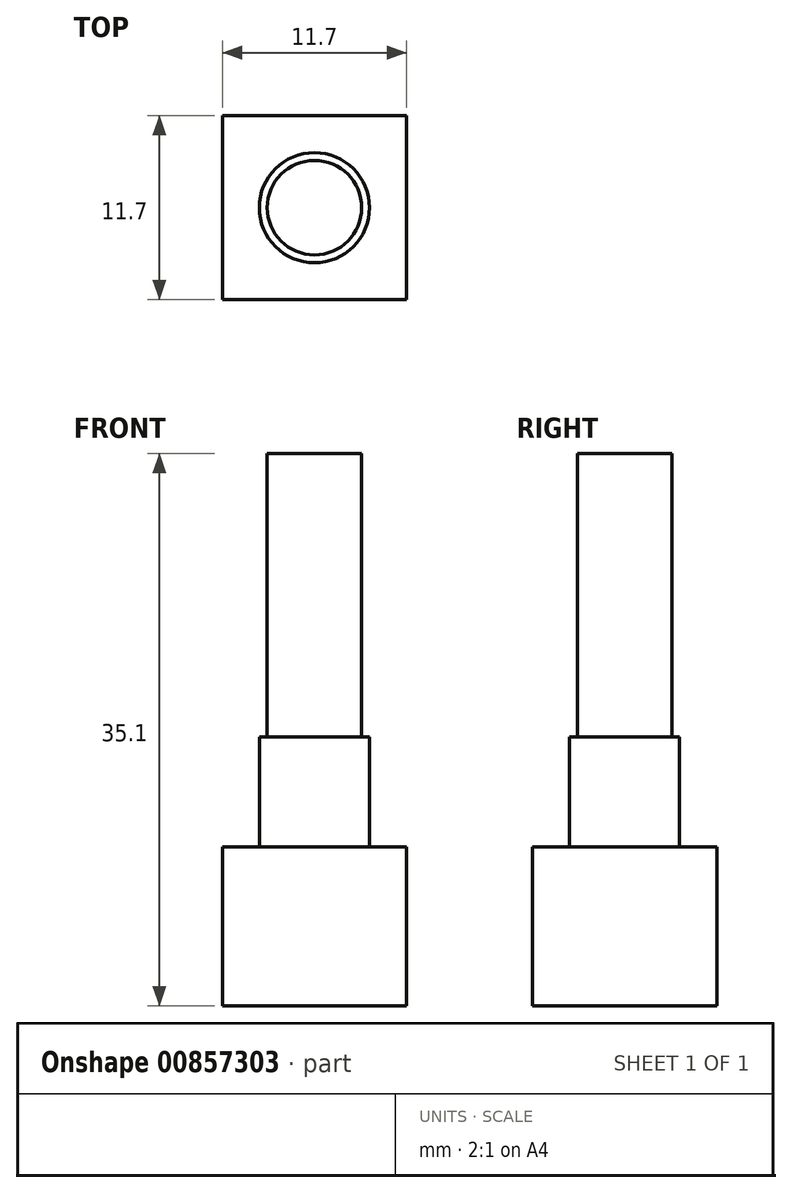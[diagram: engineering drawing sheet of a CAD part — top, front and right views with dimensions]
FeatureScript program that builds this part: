
annotation { "Feature Type Name" : "Feature", "Feature Type Description" : "" }
export const myFeature = defineFeature(function(context is Context, id is Id, definition is map)
    precondition{}
    {
        {
            var Q0;
            Q0=qCreatedBy(makeId("Top.planeOp"),FACE);
            var sketch = newSketch(context, id + "F0", { "sketchPlane" : qUnion([Q0])});
            skCircle(sketch, "E0", {"center": v(0, 0) * mm, "radius": 3 * mm});
            skSolve(sketch);
        }
        {
            var Q0;
            Q0 = qSketchRegion(id + "F0", true);
            extrude(context, id + "F1", {"entities" : qUnion([Q0]), "depth" : (7 + 11) * mm, "offsetDistance" : 25 * mm});
        }
        {
            var Q0;
            Q0=makeQuery(id+"F1.opExtrude","CAP_FACE",FACE,{"disambiguationData":[OSD([sQuery(id+"F0.wireOp",EDGE,"E0")])],"isStart":true});
            var sketch = newSketch(context, id + "F2", { "sketchPlane" : qUnion([Q0])});
            skCircle(sketch, "E1", {"center": v(0, 0) * mm, "radius": 3.5 * mm});
            skSolve(sketch);
        }
        {
            var Q0;
            Q0=makeQuery(id+"F2.imprint","IMPRINT",FACE,{"disambiguationData":[TD([[makeQuery(id+"F2.imprint","IMPRINT",EDGE,{"derivedFrom":sQuery(id+"F2.wireOp",EDGE,"E1")}),1.0]])]});
            var Q1;
            Q1=makeQuery(id+"F2.imprint","IMPRINT",FACE,{"disambiguationData":[TD([[makeQuery(id+"F2.imprint","IMPRINT",EDGE,{"derivedFrom":makeQuery(id+"F1.opExtrude","CAP_EDGE",EDGE,{"disambiguationData":[OSD([sQuery(id+"F0.wireOp",EDGE,"E0")])],"isStart":true})}),-1.0]])]});
            var Q2;
            Q2=sQuery(id+"F2.wireOp",EDGE,"E1");
            extrude(context, id + "F3", {"entities" : qUnion([Q0, Q1]), "operationType" : NewBodyOperationType.ADD, "surfaceEntities" : qUnion([Q2]), "depth" : 7 * mm, "offsetDistance" : 25 * mm});
        }
        {
            var Q0;
            Q0=makeQuery(id+"F3.opExtrude","CAP_FACE",FACE,{"disambiguationData":[OSD([sQuery(id+"F2.wireOp",EDGE,"E1")])],"isStart":false});
            var sketch = newSketch(context, id + "F4", { "sketchPlane" : qUnion([Q0])});
            skLineSegment(sketch, "E2.bottom", {"start": v(5.85, -5.85) * mm, "end": v(-5.85, -5.85) * mm});
            skLineSegment(sketch, "E2.top", {"start": v(5.85, 5.85) * mm, "end": v(-5.85, 5.85) * mm});
            skLineSegment(sketch, "E2.left", {"start": v(5.85, -5.85) * mm, "end": v(5.85, 5.85) * mm});
            skLineSegment(sketch, "E2.right", {"start": v(-5.85, -5.85) * mm, "end": v(-5.85, 5.85) * mm});
            skPoint(sketch, "E2.middle", {"position": v(0, 0) * mm});
            skSolve(sketch);
        }
        {
            var Q0;
            Q0=makeQuery(id+"F4.imprint","IMPRINT",FACE,{"disambiguationData":[TD([[makeQuery(id+"F4.imprint","IMPRINT",EDGE,{"derivedFrom":sQuery(id+"F4.wireOp",EDGE,"E2.bottom")}),-1.0]])]});
            var Q1;
            Q1=makeQuery(id+"F4.imprint","IMPRINT",FACE,{"disambiguationData":[TD([[makeQuery(id+"F4.imprint","IMPRINT",EDGE,{"derivedFrom":makeQuery(id+"F3.opExtrude","CAP_EDGE",EDGE,{"disambiguationData":[OSD([sQuery(id+"F2.wireOp",EDGE,"E1")])],"isStart":false})}),1.0]])]});
            extrude(context, id + "F5", {"entities" : qUnion([Q0, Q1]), "operationType" : NewBodyOperationType.ADD, "depth" : (6.6 + 3.5) * mm, "offsetDistance" : 25 * mm});
        }
    });
